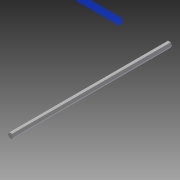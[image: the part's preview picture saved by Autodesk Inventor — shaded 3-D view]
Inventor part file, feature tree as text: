
AUTODESK INVENTOR PART (.ipt)
format: ipt  version: 2014 (Build 180170000, 170)  size: 77,312 bytes
history: native  units: in
note: dims shown in document units (in); Inventor stores cm internally (conversion verified against a paired STEP export)
features: extrude x1, sketch x1
ambient origin geometry x8: Origin, YZ Plane, XZ Plane, XY Plane, X Axis, Y Axis, Z Axis, Center Point
bodies: Solid1 (feature_tree)
feature tree (2):
  extrude  "Extrusion1"  Depth=17.0in TaperAngle=0.0deg
  sketch  "Sketch1"  dims[d0=0.5in d1=17.0in d2=0.0in]
